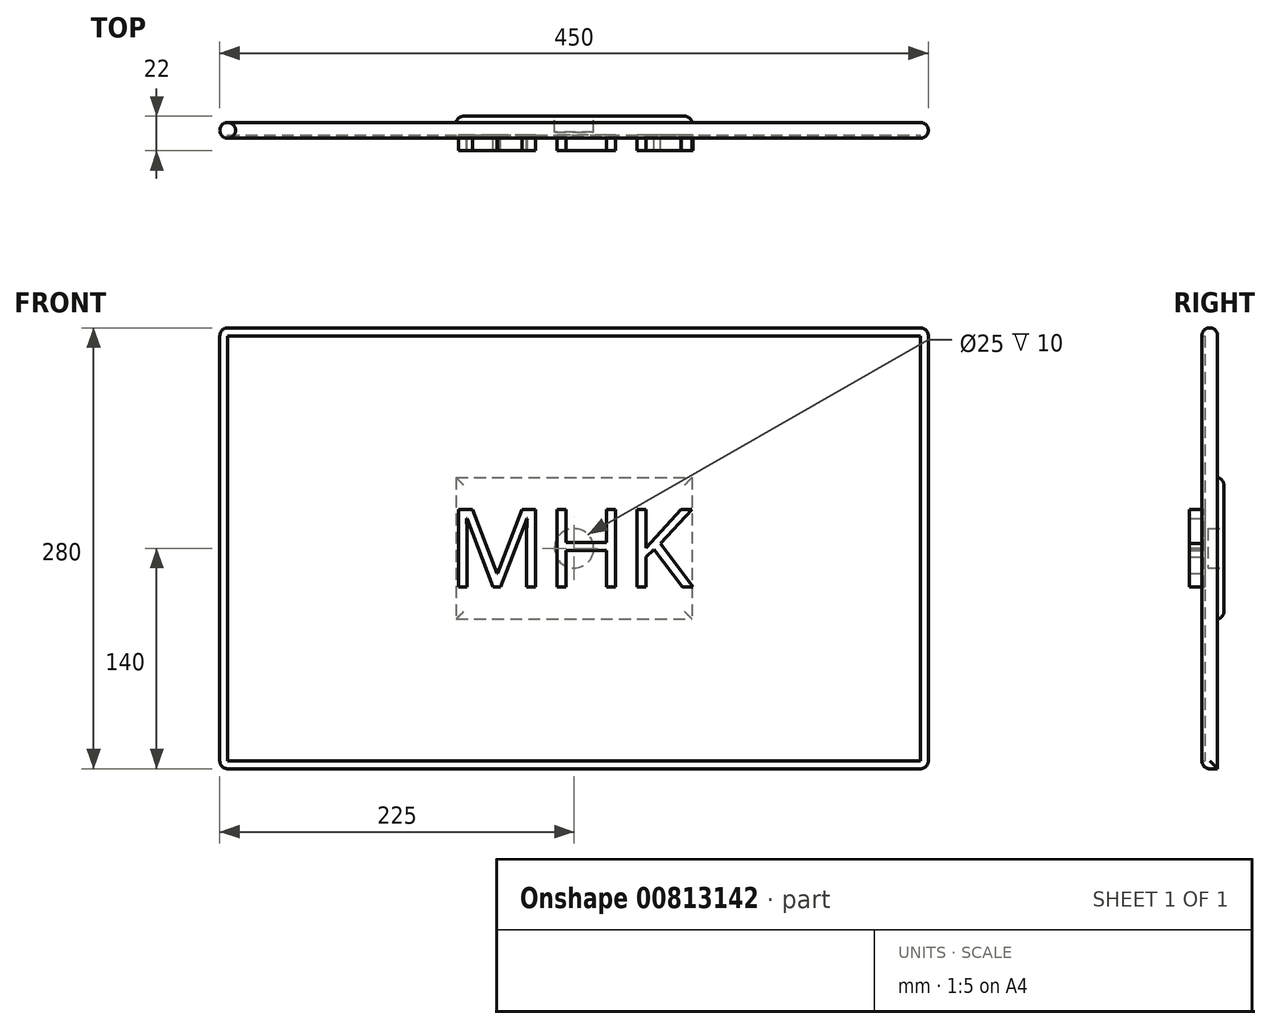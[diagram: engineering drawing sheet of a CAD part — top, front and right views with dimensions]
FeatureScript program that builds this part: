
annotation { "Feature Type Name" : "Feature", "Feature Type Description" : "" }
export const myFeature = defineFeature(function(context is Context, id is Id, definition is map)
    precondition{}
    {
        {
            var Q0;
            Q0=qCreatedBy(makeId("Front.planeOp"),FACE);
            var sketch = newSketch(context, id + "F0", { "sketchPlane" : qUnion([Q0])});
            skLineSegment(sketch, "E0.bottom", {"start": v(-225, 140) * mm, "end": v(225, 140) * mm});
            skLineSegment(sketch, "E0.top", {"start": v(-225, -140) * mm, "end": v(225, -140) * mm});
            skLineSegment(sketch, "E0.left", {"start": v(-225, 140) * mm, "end": v(-225, -140) * mm});
            skLineSegment(sketch, "E0.right", {"start": v(225, 140) * mm, "end": v(225, -140) * mm});
            skLineSegment(sketch, "E1.0", {"start": v(-220, 135) * mm, "end": v(220, 135) * mm});
            skLineSegment(sketch, "E2.0", {"start": v(-220, 135) * mm, "end": v(-220, -135) * mm});
            skLineSegment(sketch, "E3.0", {"start": v(-220, -135) * mm, "end": v(220, -135) * mm});
            skLineSegment(sketch, "E4.0", {"start": v(220, 135) * mm, "end": v(220, -135) * mm});
            skLineSegment(sketch, "E5.bottom", {"start": v(-75, 45) * mm, "end": v(75, 45) * mm});
            skLineSegment(sketch, "E5.top", {"start": v(-75, -45) * mm, "end": v(75, -45) * mm});
            skLineSegment(sketch, "E5.left", {"start": v(-75, 45) * mm, "end": v(-75, -45) * mm});
            skLineSegment(sketch, "E5.right", {"start": v(75, 45) * mm, "end": v(75, -45) * mm});
            skSolve(sketch);
        }
        {
            var Q0;
            Q0=makeQuery(id+"F0.imprint","IMPRINT",FACE,{"disambiguationData":[TD([[makeQuery(id+"F0.imprint","IMPRINT",EDGE,{"derivedFrom":sQuery(id+"F0.wireOp",EDGE,"E1.0")}),-1.0]])]});
            var Q1;
            Q1=makeQuery(id+"F0.imprint","IMPRINT",FACE,{"disambiguationData":[TD([[makeQuery(id+"F0.imprint","IMPRINT",EDGE,{"derivedFrom":sQuery(id+"F0.wireOp",EDGE,"E5.bottom")}),-1.0]])]});
            extrude(context, id + "F1", {"entities" : qUnion([Q0, Q1]), "depth" : 8 * mm, "offsetDistance" : 25 * mm});
        }
        {
            var Q0;
            Q0=makeQuery(id+"F0.imprint","IMPRINT",FACE,{"disambiguationData":[TD([[makeQuery(id+"F0.imprint","IMPRINT",EDGE,{"derivedFrom":sQuery(id+"F0.wireOp",EDGE,"E0.bottom")}),-1.0]])]});
            extrude(context, id + "F2", {"entities" : qUnion([Q0]), "operationType" : NewBodyOperationType.ADD, "depth" : 10 * mm, "offsetDistance" : 25 * mm});
        }
        {
            var Q0;
            Q0=makeQuery(id+"F0.imprint","IMPRINT",FACE,{"disambiguationData":[TD([[makeQuery(id+"F0.imprint","IMPRINT",EDGE,{"derivedFrom":sQuery(id+"F0.wireOp",EDGE,"E5.bottom")}),-1.0]])]});
            extrude(context, id + "F3", {"entities" : qUnion([Q0]), "operationType" : NewBodyOperationType.ADD, "oppositeDirection" : true, "depth" : 4 * mm, "offsetDistance" : 25 * mm});
        }
        {
            var Q0;
            Q0=makeQuery(id+"F2.opExtrude","CAP_EDGE",EDGE,{"disambiguationData":[OSD([sQuery(id+"F0.wireOp",EDGE,"E0.bottom")])],"isStart":false});
            var Q1;
            Q1=makeQuery(id+"F2.opExtrude","CAP_EDGE",EDGE,{"disambiguationData":[OSD([sQuery(id+"F0.wireOp",EDGE,"E0.left")])],"isStart":false});
            var Q2;
            Q2=makeQuery(id+"F2.opExtrude","SWEPT_EDGE",EDGE,{"disambiguationData":[OSD([sQuery(id+"F0.wireOp",EDGE,"E0.bottom"),sQuery(id+"F0.wireOp",EDGE,"E0.left")])]});
            var Q3;
            Q3=makeQuery(id+"F2.opExtrude","SWEPT_EDGE",EDGE,{"disambiguationData":[OSD([sQuery(id+"F0.wireOp",EDGE,"E0.bottom"),sQuery(id+"F0.wireOp",EDGE,"E0.right")])]});
            var Q4;
            Q4=makeQuery(id+"F2.opExtrude","SWEPT_EDGE",EDGE,{"disambiguationData":[OSD([sQuery(id+"F0.wireOp",EDGE,"E0.top"),sQuery(id+"F0.wireOp",EDGE,"E0.right")])]});
            var Q5;
            Q5=makeQuery(id+"F2.opExtrude","CAP_EDGE",EDGE,{"disambiguationData":[OSD([sQuery(id+"F0.wireOp",EDGE,"E0.right")])],"isStart":false});
            var Q6;
            Q6=makeQuery(id+"F2.opExtrude","CAP_EDGE",EDGE,{"disambiguationData":[OSD([sQuery(id+"F0.wireOp",EDGE,"E0.top")])],"isStart":false});
            var Q7;
            Q7=makeQuery(id+"F2.opExtrude","SWEPT_EDGE",EDGE,{"disambiguationData":[OSD([sQuery(id+"F0.wireOp",EDGE,"E0.top"),sQuery(id+"F0.wireOp",EDGE,"E0.left")])]});
            var Q8;
            Q8=makeQuery(id+"F2.opExtrude","CAP_EDGE",EDGE,{"disambiguationData":[OSD([sQuery(id+"F0.wireOp",EDGE,"E0.bottom")])],"isStart":true});
            var Q9;
            Q9=makeQuery(id+"F2.opExtrude","CAP_EDGE",EDGE,{"disambiguationData":[OSD([sQuery(id+"F0.wireOp",EDGE,"E0.left")])],"isStart":true});
            var Q10;
            Q10=makeQuery(id+"F2.opExtrude","CAP_EDGE",EDGE,{"disambiguationData":[OSD([sQuery(id+"F0.wireOp",EDGE,"E0.right")])],"isStart":true});
            fillet(context, id + "F4", {"entities" : qUnion([Q0, Q1, Q2, Q3, Q4, Q5, Q6, Q7, Q8, Q9, Q10]), "radius" : 5 * mm, "tangentPropagation" : true, "allowEdgeOverflow" : false});
        }
        {
            var Q0;
            Q0=makeQuery(id+"F3.opExtrude","CAP_FACE",FACE,{"disambiguationData":[OSD([sQuery(id+"F0.wireOp",EDGE,"E5.bottom"),sQuery(id+"F0.wireOp",EDGE,"E5.top"),sQuery(id+"F0.wireOp",EDGE,"E5.left"),sQuery(id+"F0.wireOp",EDGE,"E5.right")])],"isStart":false});
            fillet(context, id + "F5", {"entities" : qUnion([Q0]), "radius" : 5 * mm, "tangentPropagation" : true, "allowEdgeOverflow" : false});
        }
        {
            var Q0;
            Q0=makeQuery(id+"F3.opExtrude","CAP_FACE",FACE,{"disambiguationData":[OSD([sQuery(id+"F0.wireOp",EDGE,"E5.bottom"),sQuery(id+"F0.wireOp",EDGE,"E5.top"),sQuery(id+"F0.wireOp",EDGE,"E5.left"),sQuery(id+"F0.wireOp",EDGE,"E5.right")])],"isStart":false});
            var sketch = newSketch(context, id + "F6", { "sketchPlane" : qUnion([Q0])});
            skCircle(sketch, "E6", {"center": v(0, 0) * mm, "radius": 12.5 * mm});
            skSolve(sketch);
        }
        {
            var Q0;
            Q0=makeQuery(id+"F6.imprint","IMPRINT",FACE,{"disambiguationData":[TD([[makeQuery(id+"F6.imprint","IMPRINT",EDGE,{"derivedFrom":sQuery(id+"F6.wireOp",EDGE,"E6")}),1.0]])]});
            extrude(context, id + "F7", {"entities" : qUnion([Q0]), "operationType" : NewBodyOperationType.REMOVE, "oppositeDirection" : true, "depth" : 10 * mm, "offsetDistance" : 25 * mm});
        }
        {
            var Q0;
            Q0=makeQuery(id+"F1.opExtrude","CAP_FACE",FACE,{"disambiguationData":[OSD([sQuery(id+"F0.wireOp",EDGE,"E1.0"),sQuery(id+"F0.wireOp",EDGE,"E2.0"),sQuery(id+"F0.wireOp",EDGE,"E3.0"),sQuery(id+"F0.wireOp",EDGE,"E4.0")])],"isStart":false});
            var sketch = newSketch(context, id + "F8", { "sketchPlane" : qUnion([Q0])});
            skText(sketch, "E7", { "text": "MHK", "fontName": "OpenSans-Regular.ttf"});
            const initialGuessF8  = {"E7": [-0.08, -0.02467, 1, 0, 0.04967]};
            skSetInitialGuess(sketch, initialGuessF8);
            skSolve(sketch);
        }
        {
            var Q0;
            Q0 = qSketchRegion(id + "F8", true);
            extrude(context, id + "F9", {"entities" : qUnion([Q0]), "operationType" : NewBodyOperationType.ADD, "depth" : 10 * mm, "offsetDistance" : 25 * mm});
        }
    });
